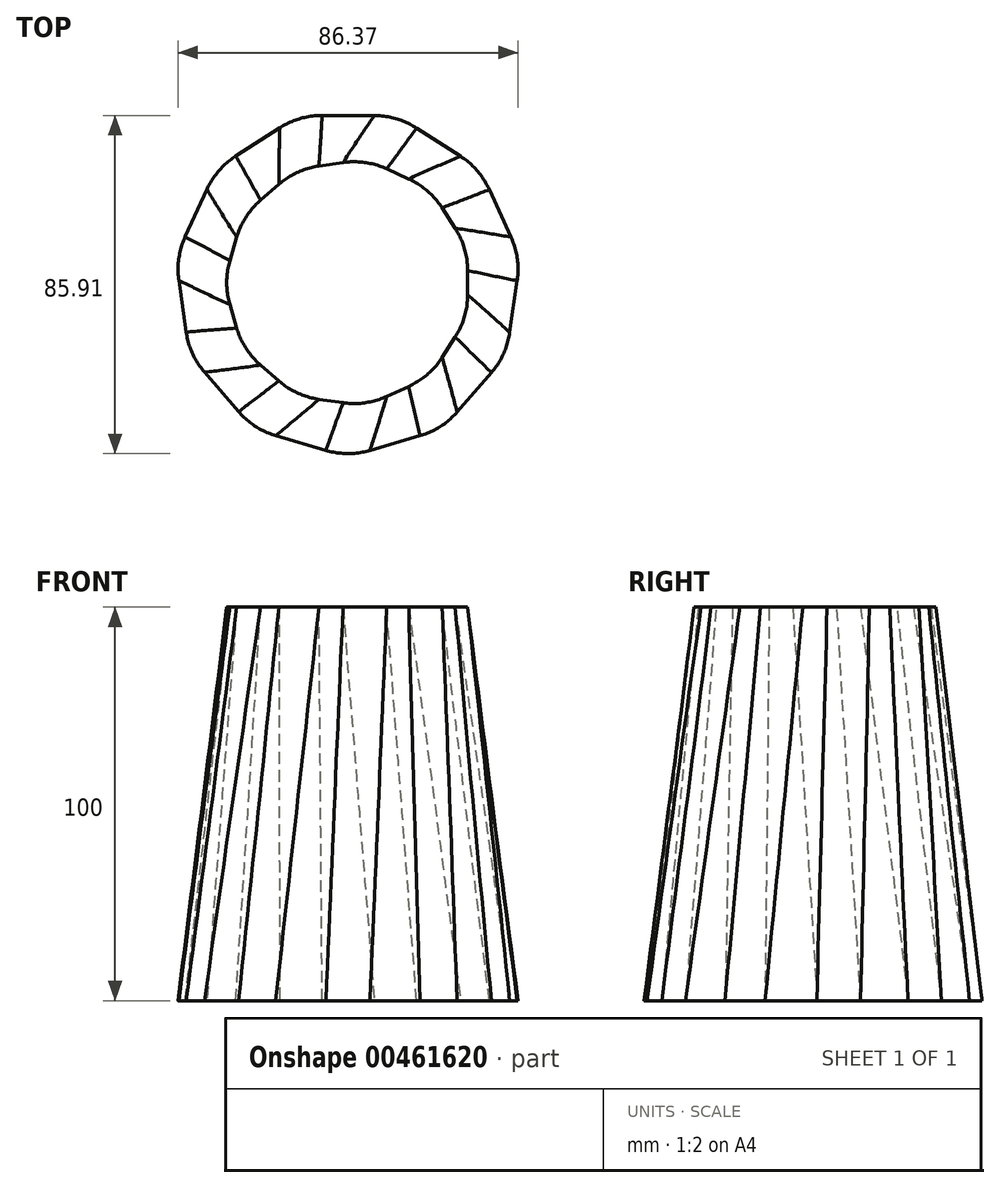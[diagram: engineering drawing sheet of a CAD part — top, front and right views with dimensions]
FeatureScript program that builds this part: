
annotation { "Feature Type Name" : "Feature", "Feature Type Description" : "" }
export const myFeature = defineFeature(function(context is Context, id is Id, definition is map)
    precondition{}
    {
        {
            var Q0;
            Q0=qCreatedBy(makeId("Top.planeOp"),FACE);
            var sketch = newSketch(context, id + "F0", { "sketchPlane" : qUnion([Q0])});
            skLineSegment(sketch, "E0.0", {"start": v(33.49, 28.95) * mm, "end": v(43.82, 6.25) * mm});
            skLineSegment(sketch, "E0.1", {"start": v(43.82, 6.25) * mm, "end": v(40.24, -18.44) * mm});
            skLineSegment(sketch, "E0.2", {"start": v(40.24, -18.44) * mm, "end": v(23.89, -37.27) * mm});
            skLineSegment(sketch, "E0.3", {"start": v(23.89, -37.27) * mm, "end": v(-0.05, -44.26) * mm});
            skLineSegment(sketch, "E0.4", {"start": v(-0.05, -44.26) * mm, "end": v(-23.98, -37.2) * mm});
            skLineSegment(sketch, "E0.5", {"start": v(-23.98, -37.2) * mm, "end": v(-40.29, -18.34) * mm});
            skLineSegment(sketch, "E0.6", {"start": v(-40.29, -18.34) * mm, "end": v(-43.8, 6.35) * mm});
            skLineSegment(sketch, "E0.7", {"start": v(-43.8, 6.35) * mm, "end": v(-33.42, 29.03) * mm});
            skLineSegment(sketch, "E0.8", {"start": v(-33.42, 29.03) * mm, "end": v(-12.42, 42.49) * mm});
            skLineSegment(sketch, "E0.9", {"start": v(-12.42, 42.49) * mm, "end": v(12.52, 42.46) * mm});
            skLineSegment(sketch, "E0.10", {"start": v(12.52, 42.46) * mm, "end": v(33.49, 28.95) * mm});
            skPoint(sketch, "E0.0.midPoint", {"position": v(38.65, 17.6) * mm});
            skSolve(sketch);
        }
        {
            var Q0;
            Q0=qCreatedBy(makeId("Top.planeOp"),FACE);
            cPlane(context, id + "F1", {"entities" : qUnion([Q0]), "cplaneType" : CPlaneType.OFFSET, "offset" : 100 * mm, "width" : 150 * mm, "height" : 150 * mm});
        }
        {
            var Q0;
            Q0=qCreatedBy(id+"F1.planeOp",FACE);
            var sketch = newSketch(context, id + "F2", { "sketchPlane" : qUnion([Q0])});
            skLineSegment(sketch, "E1.0", {"start": v(30.38, 8.92) * mm, "end": v(30.38, -8.92) * mm});
            skLineSegment(sketch, "E1.1", {"start": v(30.38, -8.92) * mm, "end": v(20.74, -23.93) * mm});
            skLineSegment(sketch, "E1.2", {"start": v(20.74, -23.93) * mm, "end": v(4.5, -31.35) * mm});
            skLineSegment(sketch, "E1.3", {"start": v(4.5, -31.35) * mm, "end": v(-13.16, -28.8) * mm});
            skLineSegment(sketch, "E1.4", {"start": v(-13.16, -28.8) * mm, "end": v(-26.64, -17.12) * mm});
            skLineSegment(sketch, "E1.5", {"start": v(-26.64, -17.12) * mm, "end": v(-31.67, 0) * mm});
            skLineSegment(sketch, "E1.6", {"start": v(-31.67, 0) * mm, "end": v(-26.64, 17.12) * mm});
            skLineSegment(sketch, "E1.7", {"start": v(-26.64, 17.12) * mm, "end": v(-13.16, 28.8) * mm});
            skLineSegment(sketch, "E1.8", {"start": v(-13.16, 28.8) * mm, "end": v(4.5, 31.35) * mm});
            skLineSegment(sketch, "E1.9", {"start": v(4.5, 31.35) * mm, "end": v(20.74, 23.93) * mm});
            skLineSegment(sketch, "E1.10", {"start": v(20.74, 23.93) * mm, "end": v(30.38, 8.92) * mm});
            skPoint(sketch, "E1.0.midPoint", {"position": v(30.38, 0) * mm});
            skPoint(sketch, "E1.cCircle.center.orphan", {"position": v(0, 0) * mm});
            skSolve(sketch);
        }
        {
            var Q0;
            Q0=makeQuery(id+"F2.imprint","IMPRINT",FACE,{"disambiguationData":[TD([[makeQuery(id+"F2.imprint","IMPRINT",EDGE,{"derivedFrom":sQuery(id+"F2.wireOp",EDGE,"E1.0")}),-1.0]])]});
            var Q1;
            Q1=makeQuery(id+"F0.imprint","IMPRINT",FACE,{"disambiguationData":[TD([[makeQuery(id+"F0.imprint","IMPRINT",EDGE,{"derivedFrom":sQuery(id+"F0.wireOp",EDGE,"E0.0")}),-1.0]])]});
            loft(context, id + "F3", {"sheetProfilesArray" : [{ "sheetProfileEntities" : qUnion([Q0]) }, { "sheetProfileEntities" : qUnion([Q1]) }]});
        }
        {
            var Q0;
            Q0=makeQuery(id+"F3.opLoft","SWEPT_EDGE",EDGE,{"disambiguationData":[OSD([sQuery(id+"F0.wireOp",EDGE,"E0.6"),sQuery(id+"F0.wireOp",EDGE,"E0.7"),sQuery(id+"F2.wireOp",EDGE,"E1.5"),sQuery(id+"F2.wireOp",EDGE,"E1.6")])]});
            var Q1;
            Q1=makeQuery(id+"F3.opLoft","SWEPT_EDGE",EDGE,{"disambiguationData":[OSD([sQuery(id+"F0.wireOp",EDGE,"E0.5"),sQuery(id+"F0.wireOp",EDGE,"E0.6"),sQuery(id+"F2.wireOp",EDGE,"E1.4"),sQuery(id+"F2.wireOp",EDGE,"E1.5")])]});
            var Q2;
            Q2=makeQuery(id+"F3.opLoft","SWEPT_EDGE",EDGE,{"disambiguationData":[OSD([sQuery(id+"F0.wireOp",EDGE,"E0.7"),sQuery(id+"F0.wireOp",EDGE,"E0.8"),sQuery(id+"F2.wireOp",EDGE,"E1.6"),sQuery(id+"F2.wireOp",EDGE,"E1.7")])]});
            var Q3;
            Q3=makeQuery(id+"F3.opLoft","SWEPT_EDGE",EDGE,{"disambiguationData":[OSD([sQuery(id+"F0.wireOp",EDGE,"E0.8"),sQuery(id+"F0.wireOp",EDGE,"E0.9"),sQuery(id+"F2.wireOp",EDGE,"E1.7"),sQuery(id+"F2.wireOp",EDGE,"E1.8")])]});
            var Q4;
            Q4=makeQuery(id+"F3.opLoft","SWEPT_EDGE",EDGE,{"disambiguationData":[OSD([sQuery(id+"F0.wireOp",EDGE,"E0.9"),sQuery(id+"F0.wireOp",EDGE,"E0.10"),sQuery(id+"F2.wireOp",EDGE,"E1.8"),sQuery(id+"F2.wireOp",EDGE,"E1.9")])]});
            var Q5;
            Q5=makeQuery(id+"F3.opLoft","SWEPT_EDGE",EDGE,{"disambiguationData":[OSD([sQuery(id+"F0.wireOp",EDGE,"E0.0"),sQuery(id+"F0.wireOp",EDGE,"E0.10"),sQuery(id+"F2.wireOp",EDGE,"E1.9"),sQuery(id+"F2.wireOp",EDGE,"E1.10")])]});
            var Q6;
            Q6=makeQuery(id+"F3.opLoft","SWEPT_EDGE",EDGE,{"disambiguationData":[OSD([sQuery(id+"F0.wireOp",EDGE,"E0.0"),sQuery(id+"F0.wireOp",EDGE,"E0.1"),sQuery(id+"F2.wireOp",EDGE,"E1.0"),sQuery(id+"F2.wireOp",EDGE,"E1.10")])]});
            var Q7;
            Q7=makeQuery(id+"F3.opLoft","SWEPT_EDGE",EDGE,{"disambiguationData":[OSD([sQuery(id+"F0.wireOp",EDGE,"E0.1"),sQuery(id+"F0.wireOp",EDGE,"E0.2"),sQuery(id+"F2.wireOp",EDGE,"E1.0"),sQuery(id+"F2.wireOp",EDGE,"E1.1")])]});
            var Q8;
            Q8=makeQuery(id+"F3.opLoft","SWEPT_EDGE",EDGE,{"disambiguationData":[OSD([sQuery(id+"F0.wireOp",EDGE,"E0.2"),sQuery(id+"F0.wireOp",EDGE,"E0.3"),sQuery(id+"F2.wireOp",EDGE,"E1.1"),sQuery(id+"F2.wireOp",EDGE,"E1.2")])]});
            var Q9;
            Q9=makeQuery(id+"F3.opLoft","SWEPT_EDGE",EDGE,{"disambiguationData":[OSD([sQuery(id+"F0.wireOp",EDGE,"E0.3"),sQuery(id+"F0.wireOp",EDGE,"E0.4"),sQuery(id+"F2.wireOp",EDGE,"E1.2"),sQuery(id+"F2.wireOp",EDGE,"E1.3")])]});
            var Q10;
            Q10=makeQuery(id+"F3.opLoft","SWEPT_EDGE",EDGE,{"disambiguationData":[OSD([sQuery(id+"F0.wireOp",EDGE,"E0.4"),sQuery(id+"F0.wireOp",EDGE,"E0.5"),sQuery(id+"F2.wireOp",EDGE,"E1.3"),sQuery(id+"F2.wireOp",EDGE,"E1.4")])]});
            fillet(context, id + "F4", {"entities" : qUnion([Q0, Q1, Q2, Q3, Q4, Q5, Q6, Q7, Q8, Q9, Q10]), "radius" : 20 * mm, "tangentPropagation" : true, "allowEdgeOverflow" : false});
        }
    });
